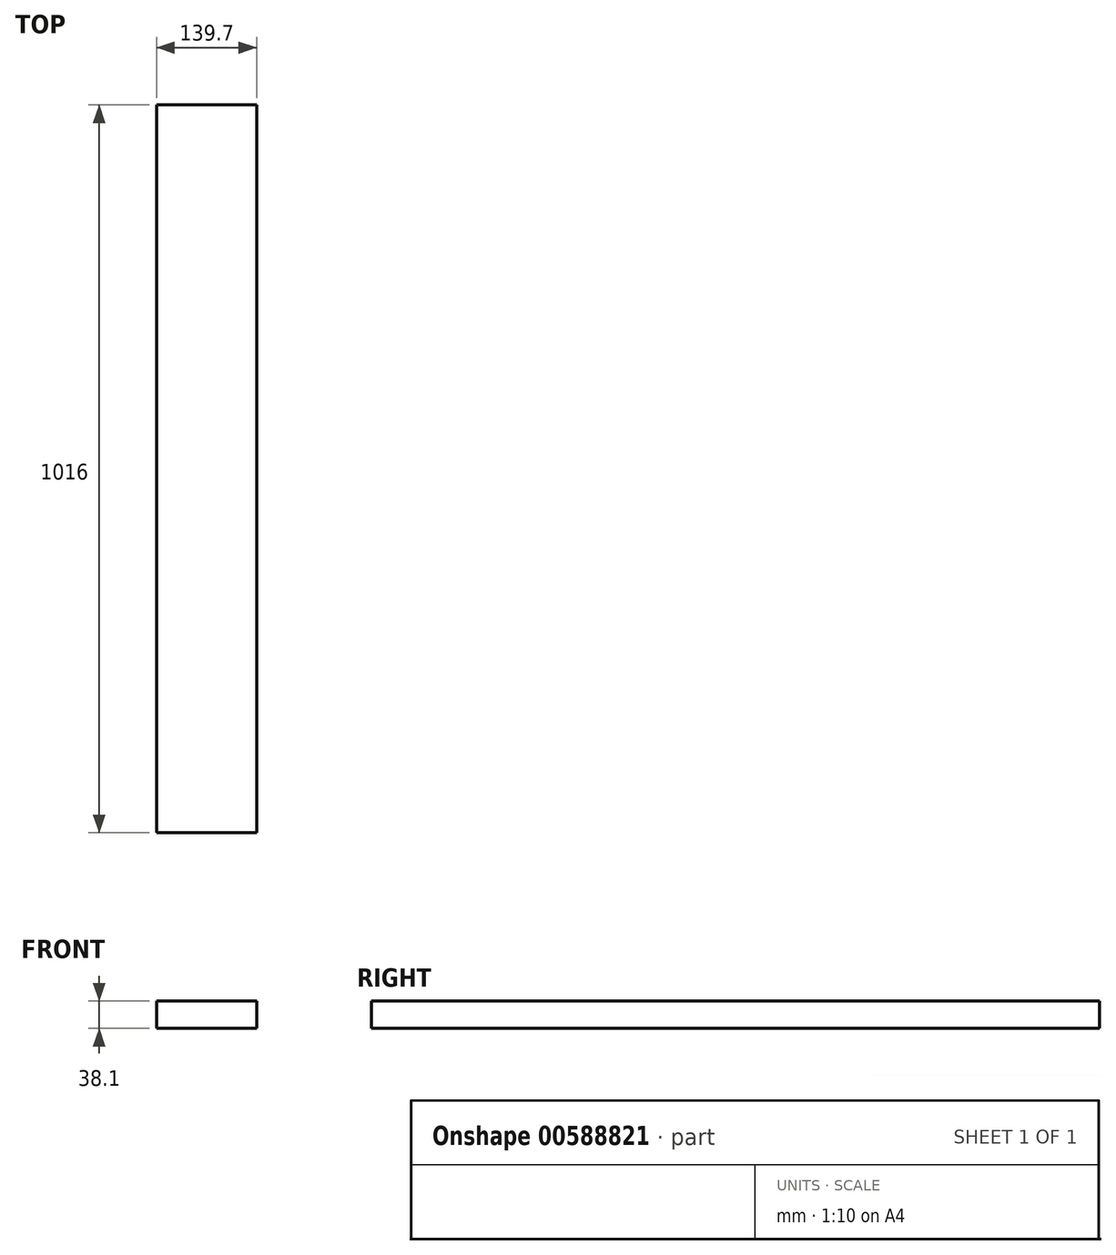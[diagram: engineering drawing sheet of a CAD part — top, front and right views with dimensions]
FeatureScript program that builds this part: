
annotation { "Feature Type Name" : "Feature", "Feature Type Description" : "" }
export const myFeature = defineFeature(function(context is Context, id is Id, definition is map)
    precondition{}
    {
        {
            var Q0;
            Q0=qCreatedBy(makeId("Front.planeOp"),FACE);
            var sketch = newSketch(context, id + "F0", { "sketchPlane" : qUnion([Q0])});
            skLineSegment(sketch, "E0.bottom", {"start": v(0, 0) * mm, "end": v(139.7, 0) * mm});
            skLineSegment(sketch, "E0.top", {"start": v(0, 38.1) * mm, "end": v(139.7, 38.1) * mm});
            skLineSegment(sketch, "E0.left", {"start": v(0, 0) * mm, "end": v(0, 38.1) * mm});
            skLineSegment(sketch, "E0.right", {"start": v(139.7, 0) * mm, "end": v(139.7, 38.1) * mm});
            skSolve(sketch);
        }
        {
            var Q0;
            Q0 = qSketchRegion(id + "F0", true);
            var Q1;
            Q1=makeQuery(id+"F0.imprint","IMPRINT",FACE,{"disambiguationData":[TD([[makeQuery(id+"F0.imprint","IMPRINT",EDGE,{"derivedFrom":sQuery(id+"F0.wireOp",EDGE,"E0.bottom")}),1.0]])]});
            extrude(context, id + "F1", {"entities" : qUnion([Q0, Q1]), "oppositeDirection" : true, "depth" : 1016 * mm, "offsetDistance" : 25.4 * mm});
        }
    });
